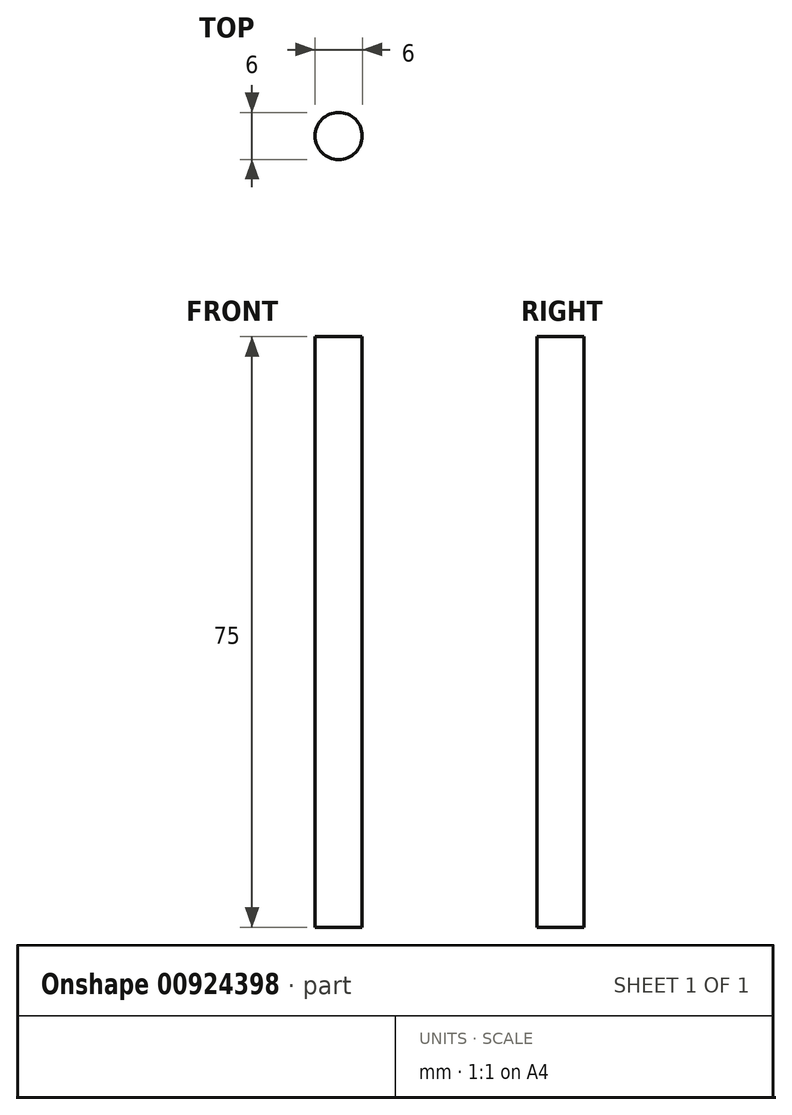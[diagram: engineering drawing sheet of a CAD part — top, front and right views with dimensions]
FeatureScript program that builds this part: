
annotation { "Feature Type Name" : "Feature", "Feature Type Description" : "" }
export const myFeature = defineFeature(function(context is Context, id is Id, definition is map)
    precondition{}
    {
        {
            var Q0;
            Q0=qCreatedBy(makeId("Top.planeOp"),FACE);
            var sketch = newSketch(context, id + "F0", { "sketchPlane" : qUnion([Q0])});
            skCircle(sketch, "E0", {"center": v(-12.8, 19.32) * mm, "radius": 3 * mm});
            skSolve(sketch);
        }
        {
            var Q0;
            Q0 = qSketchRegion(id + "F0", true);
            extrude(context, id + "F1", {"entities" : qUnion([Q0]), "depth" : 75 * mm, "offsetDistance" : 25 * mm});
        }
    });
